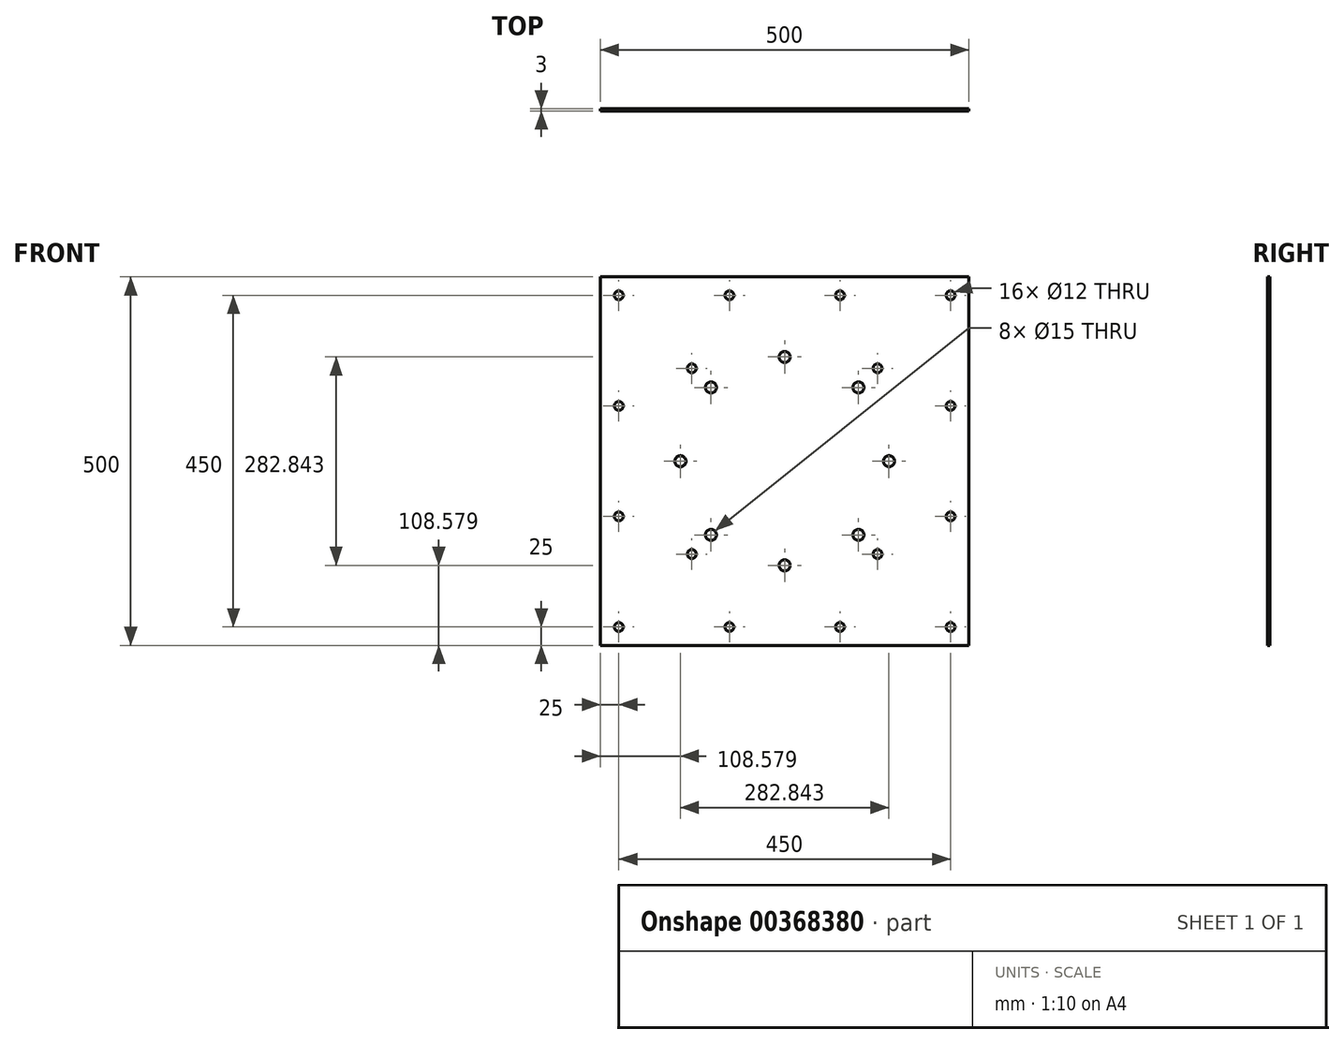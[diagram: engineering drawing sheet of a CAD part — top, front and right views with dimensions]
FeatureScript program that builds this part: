
annotation { "Feature Type Name" : "Feature", "Feature Type Description" : "" }
export const myFeature = defineFeature(function(context is Context, id is Id, definition is map)
    precondition{}
    {
        {
            var Q0;
            Q0=qCreatedBy(makeId("Front.planeOp"),FACE);
            var sketch = newSketch(context, id + "F0", { "sketchPlane" : qUnion([Q0])});
            skLineSegment(sketch, "E0.bottom", {"start": v(0, 0) * mm, "end": v(500, 0) * mm});
            skLineSegment(sketch, "E0.top", {"start": v(0, 500) * mm, "end": v(500, 500) * mm});
            skLineSegment(sketch, "E0.left", {"start": v(0, 0) * mm, "end": v(0, 500) * mm});
            skLineSegment(sketch, "E0.right", {"start": v(500, 0) * mm, "end": v(500, 500) * mm});
            skSolve(sketch);
        }
        {
            var Q0;
            Q0=qSketchRegion(id+"F0",true);
            extrude(context, id + "F1", {"entities" : qUnion([Q0]), "depth" : 3 * mm});
        }
        {
            var Q0;
            Q0=makeQuery(id+"F1.opExtrude","CAP_FACE",FACE,{"disambiguationData":[OSD([sQuery(id+"F0.wireOp",EDGE,"E0.bottom"),sQuery(id+"F0.wireOp",EDGE,"E0.top"),sQuery(id+"F0.wireOp",EDGE,"E0.left"),sQuery(id+"F0.wireOp",EDGE,"E0.right")])],"isStart":false});
            var sketch = newSketch(context, id + "F2", { "sketchPlane" : qUnion([Q0])});
            skLineSegment(sketch, "E1.bottom", {"start": v(150, 350) * mm, "end": v(350, 350) * mm});
            skLineSegment(sketch, "E1.top", {"start": v(150, 150) * mm, "end": v(350, 150) * mm});
            skLineSegment(sketch, "E1.left", {"start": v(150, 350) * mm, "end": v(150, 150) * mm});
            skLineSegment(sketch, "E1.right", {"start": v(350, 350) * mm, "end": v(350, 150) * mm});
            skLineSegment(sketch, "E2.1.0", {"start": v(108.58, 250) * mm, "end": v(250, 108.58) * mm});
            skLineSegment(sketch, "E2.1.1", {"start": v(250, 391.42) * mm, "end": v(391.42, 250) * mm});
            skLineSegment(sketch, "E2.1.2", {"start": v(250, 391.42) * mm, "end": v(108.58, 250) * mm});
            skLineSegment(sketch, "E2.1.3", {"start": v(391.42, 250) * mm, "end": v(250, 108.58) * mm});
            skPoint(sketch, "E2.center", {"position": v(250, 250) * mm});
            skLineSegment(sketch, "E2.anchor1", {"start": v(250, 250) * mm, "end": v(150, 150) * mm, "construction": true});
            skLineSegment(sketch, "E2.anchor2", {"start": v(250, 250) * mm, "end": v(108.58, 250) * mm, "construction": true});
            skLineSegment(sketch, "E3", {"start": v(0, 0) * mm, "end": v(500, 500) * mm});
            skLineSegment(sketch, "E4", {"start": v(0, 500) * mm, "end": v(500, 0) * mm});
            skSolve(sketch);
        }
        {
            var Q0;
            Q0=sQuery(id+"F2.wireOp",VERTEX,"E1.bottom.start");
            var Q1;
            Q1=sQuery(id+"F2.wireOp",VERTEX,"E2.1.2.start");
            var Q2;
            Q2=sQuery(id+"F2.wireOp",VERTEX,"E1.right.start");
            var Q3;
            Q3=sQuery(id+"F2.wireOp",VERTEX,"E2.1.3.start");
            var Q4;
            Q4=sQuery(id+"F2.wireOp",VERTEX,"E1.right.end");
            var Q5;
            Q5=sQuery(id+"F2.wireOp",VERTEX,"E2.1.3.end");
            var Q6;
            Q6=sQuery(id+"F2.wireOp",VERTEX,"E2.anchor1.end");
            var Q7;
            Q7=sQuery(id+"F2.wireOp",VERTEX,"E2.1.2.end");
            var Q8;
            Q8=makeQuery(id+"F1.opExtrude","SWEPT_BODY",BODY,{"disambiguationData":[OSD([sQuery(id+"F0.wireOp",EDGE,"E0.bottom"),sQuery(id+"F0.wireOp",EDGE,"E0.top"),sQuery(id+"F0.wireOp",EDGE,"E0.left"),sQuery(id+"F0.wireOp",EDGE,"E0.right")])]});
            hole(context, id + "F3", {"style" : HoleStyle.SIMPLE, "endStyle" : HoleEndStyle.THROUGH, "holeDiameter" : 15 * mm, "isTappedThrough" : true, "tappedDepth" : 12 * mm, "tapClearance" : 3, "locations" : qUnion([Q0, Q1, Q2, Q3, Q4, Q5, Q6, Q7]), "scope" : qUnion([Q8]), "majorDiameter" : 5 * mm});
        }
        {
            var Q0;
            Q0=makeQuery(id+"F1.opExtrude","CAP_FACE",FACE,{"disambiguationData":[OSD([sQuery(id+"F0.wireOp",EDGE,"E0.bottom"),sQuery(id+"F0.wireOp",EDGE,"E0.top"),sQuery(id+"F0.wireOp",EDGE,"E0.left"),sQuery(id+"F0.wireOp",EDGE,"E0.right")])],"isStart":false});
            var sketch = newSketch(context, id + "F4", { "sketchPlane" : qUnion([Q0])});
            skLineSegment(sketch, "E5.bottom", {"start": v(25, 475) * mm, "end": v(475, 475) * mm, "construction": true});
            skLineSegment(sketch, "E5.top", {"start": v(25, 25) * mm, "end": v(475, 25) * mm, "construction": true});
            skLineSegment(sketch, "E5.left", {"start": v(25, 475) * mm, "end": v(25, 25) * mm, "construction": true});
            skLineSegment(sketch, "E5.right", {"start": v(475, 475) * mm, "end": v(475, 25) * mm, "construction": true});
            skPoint(sketch, "E6", {"position": v(25, 325) * mm});
            skPoint(sketch, "E7", {"position": v(25, 175) * mm});
            skPoint(sketch, "E8", {"position": v(175, 25) * mm});
            skPoint(sketch, "E9", {"position": v(325, 25) * mm});
            skPoint(sketch, "E10", {"position": v(475, 175) * mm});
            skPoint(sketch, "E11", {"position": v(475, 325) * mm});
            skPoint(sketch, "E12", {"position": v(325, 475) * mm});
            skPoint(sketch, "E13", {"position": v(175, 475) * mm});
            skSolve(sketch);
        }
        {
            var Q0;
            Q0=sQuery(id+"F4.wireOp",VERTEX,"E6");
            var Q1;
            Q1=sQuery(id+"F4.wireOp",VERTEX,"E5.left.start");
            var Q2;
            Q2=sQuery(id+"F4.wireOp",VERTEX,"E13");
            var Q3;
            Q3=sQuery(id+"F4.wireOp",VERTEX,"E12");
            var Q4;
            Q4=sQuery(id+"F4.wireOp",VERTEX,"E5.right.start");
            var Q5;
            Q5=sQuery(id+"F4.wireOp",VERTEX,"E11");
            var Q6;
            Q6=sQuery(id+"F4.wireOp",VERTEX,"E10");
            var Q7;
            Q7=sQuery(id+"F4.wireOp",VERTEX,"E5.right.end");
            var Q8;
            Q8=sQuery(id+"F4.wireOp",VERTEX,"E9");
            var Q9;
            Q9=sQuery(id+"F4.wireOp",VERTEX,"E8");
            var Q10;
            Q10=sQuery(id+"F4.wireOp",VERTEX,"E5.left.end");
            var Q11;
            Q11=sQuery(id+"F4.wireOp",VERTEX,"E7");
            var Q12;
            Q12=makeQuery(id+"F1.opExtrude","SWEPT_BODY",BODY,{"disambiguationData":[OSD([sQuery(id+"F0.wireOp",EDGE,"E0.bottom"),sQuery(id+"F0.wireOp",EDGE,"E0.top"),sQuery(id+"F0.wireOp",EDGE,"E0.left"),sQuery(id+"F0.wireOp",EDGE,"E0.right")])]});
            hole(context, id + "F5", {"style" : HoleStyle.SIMPLE, "endStyle" : HoleEndStyle.THROUGH, "holeDiameter" : 12 * mm, "isTappedThrough" : true, "tappedDepth" : 12 * mm, "tapClearance" : 3, "locations" : qUnion([Q0, Q1, Q2, Q3, Q4, Q5, Q6, Q7, Q8, Q9, Q10, Q11]), "scope" : qUnion([Q12])});
        }
        {
            var Q0;
            Q0=makeQuery(id+"F1.opExtrude","CAP_FACE",FACE,{"disambiguationData":[OSD([sQuery(id+"F0.wireOp",EDGE,"E0.bottom"),sQuery(id+"F0.wireOp",EDGE,"E0.top"),sQuery(id+"F0.wireOp",EDGE,"E0.left"),sQuery(id+"F0.wireOp",EDGE,"E0.right")])],"isStart":false});
            var sketch = newSketch(context, id + "F6", { "sketchPlane" : qUnion([Q0])});
            skLineSegment(sketch, "E14.bottom", {"start": v(124, 376) * mm, "end": v(376, 376) * mm, "construction": true});
            skLineSegment(sketch, "E14.top", {"start": v(124, 124) * mm, "end": v(376, 124) * mm, "construction": true});
            skLineSegment(sketch, "E14.left", {"start": v(124, 376) * mm, "end": v(124, 124) * mm, "construction": true});
            skLineSegment(sketch, "E14.right", {"start": v(376, 376) * mm, "end": v(376, 124) * mm, "construction": true});
            skLineSegment(sketch, "E15", {"start": v(0, 500) * mm, "end": v(500, 0) * mm, "construction": true});
            skLineSegment(sketch, "E16", {"start": v(0, 0) * mm, "end": v(500, 500) * mm, "construction": true});
            skSolve(sketch);
        }
        {
            var Q0;
            Q0=sQuery(id+"F6.wireOp",VERTEX,"E14.left.start");
            var Q1;
            Q1=sQuery(id+"F6.wireOp",VERTEX,"E14.right.start");
            var Q2;
            Q2=sQuery(id+"F6.wireOp",VERTEX,"E14.right.end");
            var Q3;
            Q3=sQuery(id+"F6.wireOp",VERTEX,"E14.left.end");
            var Q4;
            Q4=makeQuery(id+"F1.opExtrude","SWEPT_BODY",BODY,{"disambiguationData":[OSD([sQuery(id+"F0.wireOp",EDGE,"E0.bottom"),sQuery(id+"F0.wireOp",EDGE,"E0.top"),sQuery(id+"F0.wireOp",EDGE,"E0.left"),sQuery(id+"F0.wireOp",EDGE,"E0.right")])]});
            hole(context, id + "F7", {"style" : HoleStyle.SIMPLE, "endStyle" : HoleEndStyle.THROUGH, "holeDiameter" : 12 * mm, "isTappedThrough" : true, "tappedDepth" : 12 * mm, "tapClearance" : 3, "locations" : qUnion([Q0, Q1, Q2, Q3]), "scope" : qUnion([Q4])});
        }
    });
